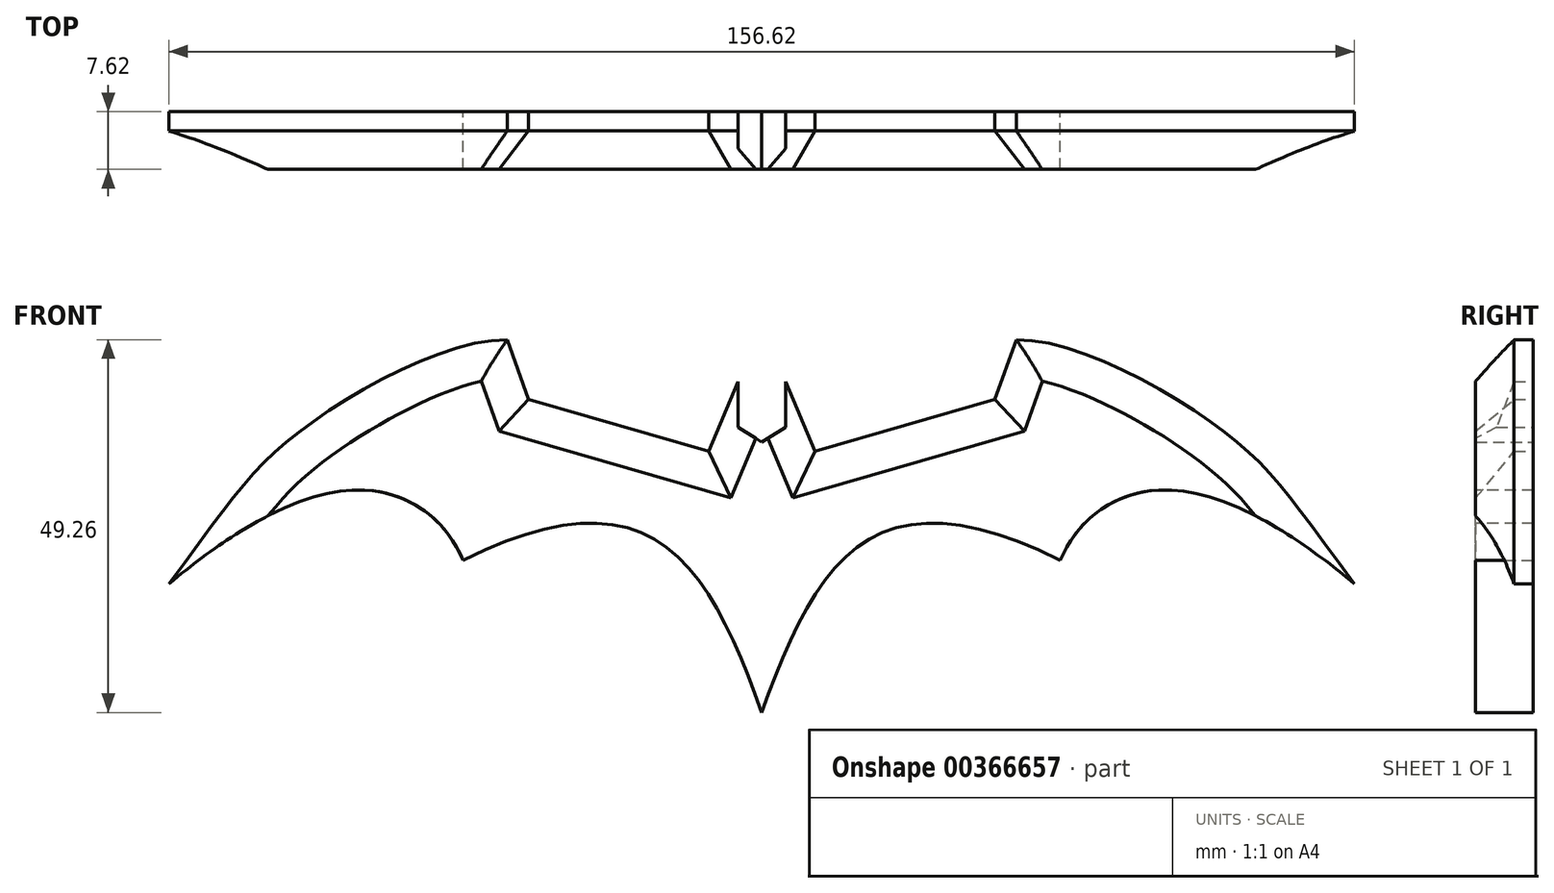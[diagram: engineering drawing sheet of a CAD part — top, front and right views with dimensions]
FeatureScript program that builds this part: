
annotation { "Feature Type Name" : "Feature", "Feature Type Description" : "" }
export const myFeature = defineFeature(function(context is Context, id is Id, definition is map)
    precondition{}
    {
        {
            var Q0;
            Q0=qCreatedBy(makeId("Front.planeOp"),FACE);
            var sketch = newSketch(context, id + "F0", { "sketchPlane" : qUnion([Q0])});
            skLineSegment(sketch, "E0", {"start": v(0, 0) * mm, "end": v(0, 35.74) * mm});
            skLineSegment(sketch, "E1", {"start": v(0, 35.74) * mm, "end": v(3.14, 37.7) * mm});
            skLineSegment(sketch, "E2", {"start": v(3.14, 37.7) * mm, "end": v(3.14, 43.7) * mm});
            skLineSegment(sketch, "E3", {"start": v(3.14, 43.7) * mm, "end": v(7.02, 34.5) * mm});
            skLineSegment(sketch, "E4", {"start": v(7.02, 34.5) * mm, "end": v(30.8, 41.36) * mm});
            skLineSegment(sketch, "E5", {"start": v(30.8, 41.36) * mm, "end": v(33.62, 49.26) * mm});
            skFitSpline(sketch, "E6", {"points": [v(33.62, 49.26) * mm, v(60.68, 37.41) * mm, v(78.3, 17) * mm], "startDerivative": vector(45.9, 0.7) * mm, "endDerivative": vector(51.14, -68.63) * mm});
            skFitSpline(sketch, "E7", {"points": [v(0, 0) * mm, v(13.37, 22.39) * mm, v(39.43, 20.09) * mm], "startDerivative": vector(20.43, 57.16) * mm, "endDerivative": vector(67.5, -34.6) * mm});
            skFitSpline(sketch, "E8", {"points": [v(39.43, 20.09) * mm, v(45.37, 27.18) * mm, v(78.3, 17) * mm], "startDerivative": vector(11.74, 26.13) * mm, "endDerivative": vector(81.37, -67.95) * mm});
            skLineSegment(sketch, "E9.MirrorCS", {"start": v(-7.02, 34.5) * mm, "end": v(-30.8, 41.36) * mm});
            skLineSegment(sketch, "E10.MirrorCS", {"start": v(0, 35.74) * mm, "end": v(-3.14, 37.7) * mm});
            skLineSegment(sketch, "E11.MirrorCS", {"start": v(-3.14, 37.7) * mm, "end": v(-3.14, 43.7) * mm});
            skLineSegment(sketch, "E12.MirrorCS", {"start": v(-3.14, 43.7) * mm, "end": v(-7.02, 34.5) * mm});
            skFitSpline(sketch, "E13.MirrorCS", {"points": [v(0, 0) * mm, v(-13.37, 22.39) * mm, v(-39.43, 20.09) * mm], "startDerivative": vector(-20.43, 57.16) * mm, "endDerivative": vector(-67.5, -34.6) * mm});
            skFitSpline(sketch, "E14.MirrorCS", {"points": [v(-39.43, 20.09) * mm, v(-45.37, 27.18) * mm, v(-78.3, 17) * mm], "startDerivative": vector(-11.74, 26.13) * mm, "endDerivative": vector(-81.37, -67.95) * mm});
            skFitSpline(sketch, "E15.MirrorCS", {"points": [v(-33.62, 49.26) * mm, v(-60.68, 37.41) * mm, v(-78.3, 17) * mm], "startDerivative": vector(-45.9, 0.7) * mm, "endDerivative": vector(-51.14, -68.63) * mm});
            skLineSegment(sketch, "E16.MirrorCS", {"start": v(-30.8, 41.36) * mm, "end": v(-33.62, 49.26) * mm});
            skSolve(sketch);
        }
        {
            var Q0;
            Q0=makeQuery(id+"F0.imprint","IMPRINT",FACE,{"disambiguationData":[TD([[makeQuery(id+"F0.imprint","IMPRINT",EDGE,{"derivedFrom":sQuery(id+"F0.wireOp",EDGE,"E0")}),1.0]])]});
            var Q1;
            Q1=makeQuery(id+"F0.imprint","IMPRINT",FACE,{"disambiguationData":[TD([[makeQuery(id+"F0.imprint","IMPRINT",EDGE,{"derivedFrom":sQuery(id+"F0.wireOp",EDGE,"E0")}),-1.0]])]});
            extrude(context, id + "F1", {"entities" : qUnion([Q0, Q1]), "depth" : 7.62 * mm});
        }
        {
            var Q0;
            Q0=makeQuery(id+"F1.opExtrude","CAP_EDGE",EDGE,{"disambiguationData":[OSD([sQuery(id+"F0.wireOp",EDGE,"E15.MirrorCS")])],"isStart":false});
            var Q1;
            Q1=makeQuery(id+"F1.opExtrude","CAP_EDGE",EDGE,{"disambiguationData":[OSD([sQuery(id+"F0.wireOp",EDGE,"E9.MirrorCS")])],"isStart":false});
            var Q2;
            Q2=makeQuery(id+"F1.opExtrude","CAP_EDGE",EDGE,{"disambiguationData":[OSD([sQuery(id+"F0.wireOp",EDGE,"E16.MirrorCS")])],"isStart":false});
            var Q3;
            Q3=makeQuery(id+"F1.opExtrude","CAP_EDGE",EDGE,{"disambiguationData":[OSD([sQuery(id+"F0.wireOp",EDGE,"E12.MirrorCS")])],"isStart":false});
            var Q4;
            Q4=makeQuery(id+"F1.opExtrude","CAP_EDGE",EDGE,{"disambiguationData":[OSD([sQuery(id+"F0.wireOp",EDGE,"E3")])],"isStart":false});
            var Q5;
            Q5=makeQuery(id+"F1.opExtrude","CAP_EDGE",EDGE,{"disambiguationData":[OSD([sQuery(id+"F0.wireOp",EDGE,"E4")])],"isStart":false});
            var Q6;
            Q6=makeQuery(id+"F1.opExtrude","CAP_EDGE",EDGE,{"disambiguationData":[OSD([sQuery(id+"F0.wireOp",EDGE,"E5")])],"isStart":false});
            var Q7;
            Q7=makeQuery(id+"F1.opExtrude","CAP_EDGE",EDGE,{"disambiguationData":[OSD([sQuery(id+"F0.wireOp",EDGE,"E6")])],"isStart":false});
            chamfer(context, id + "F2", {"entities" : qUnion([Q0, Q1, Q2, Q3, Q4, Q5, Q6, Q7]), "width" : 5.08 * mm, "tangentPropagation" : true});
        }
    });
